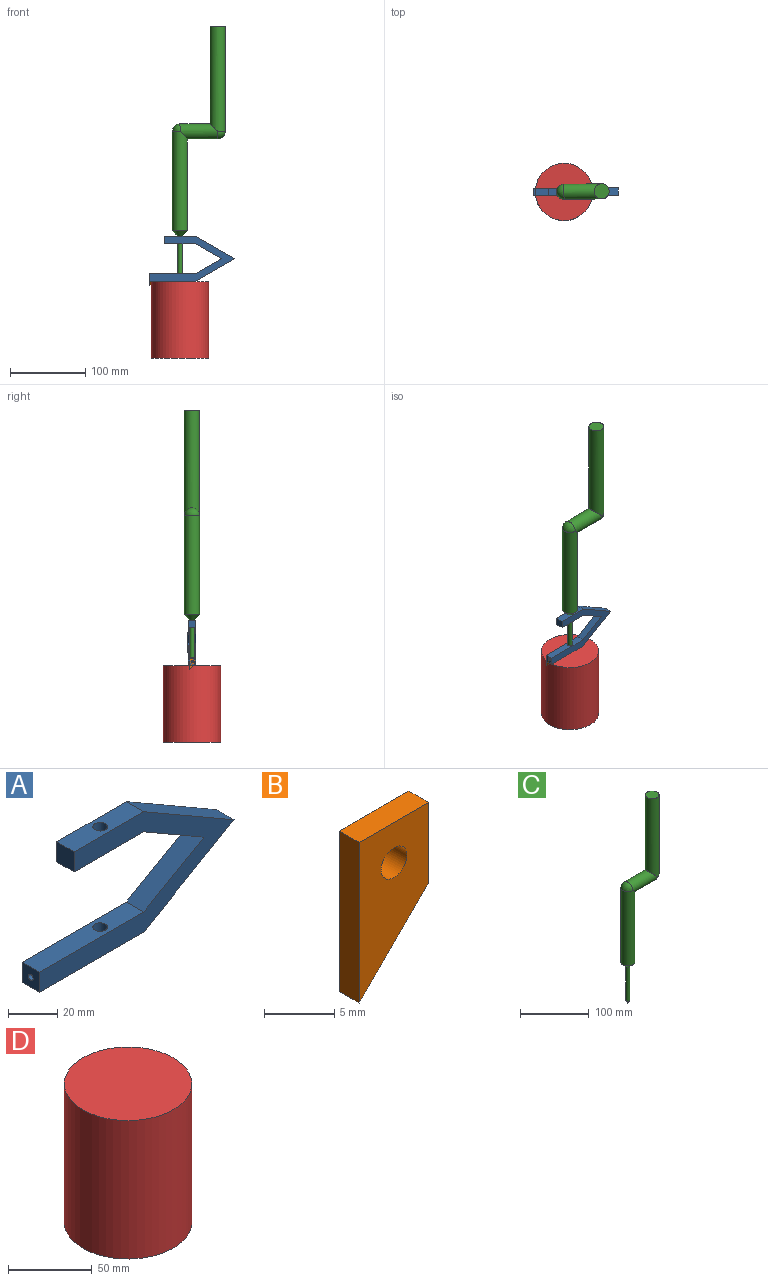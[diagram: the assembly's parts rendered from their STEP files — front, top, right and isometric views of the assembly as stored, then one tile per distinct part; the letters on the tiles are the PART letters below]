
ASSEMBLY  parts=4 mates=3
PART A: 22 faces, bbox 112x10x60 mm
  f0: plane 60x10mm, normal (0,0,-1), area 557.7mm2, adj f3,f4,f10,f11,f12,f13,f14,f15
  f1: plane 34.64x20mm, normal (-0.5,0,0.87), area 400mm2, adj f2,f9,f10,f11
  f2: plane 60x10mm, normal (0,0,1), area 571.7mm2, adj f1,f3,f10,f11,f21
  f3: plane 10x10mm, normal (-1,0,0), area 93.9mm2, adj f0,f2,f10,f11,f17
  f4: plane 51.96x30mm, normal (0.5,0,-0.87), area 600mm2, adj f0,f5,f10,f11
  f5: plane 51.96x30mm, normal (0.5,0,0.87), area 600mm2, adj f4,f6,f10,f11
  f6: plane 40x10mm, normal (0,0,1), area 371.7mm2, adj f5,f7,f10,f11,f20
  f7: plane 10x10mm, normal (-1,0,0), area 100mm2, adj f6,f8,f10,f11
  f8: plane 40x10mm, normal (0,0,-1), area 371.7mm2, adj f7,f9,f10,f11,f20
  f9: plane 34.64x20mm, normal (-0.5,0,-0.87), area 400mm2, adj f1,f8,f10,f11
  f10: plane 111.96x60mm, normal (0,-1,0), area 1866mm2, adj f0,f1,f2,f3,f4,f5,f6,f7
  f11: plane 111.96x60mm, normal (0,1,0), area 1866mm2, adj f0,f1,f2,f3,f4,f5,f6,f7
  f12: plane 7x2mm, normal (0,-1,0), area 14mm2, adj f0,f13,f15,f16
  f13: plane 7x7mm, normal (-1,0,0), area 42.9mm2, adj f0,f12,f14,f16,f18
  f14: plane 7x2mm, normal (0,1,0), area 14mm2, adj f0,f13,f15,f16
  f15: plane 7x7mm, normal (1,0,0), area 42.9mm2, adj f0,f12,f14,f16,f17
  f16: plane 7x2mm, normal (0,0,-1), area 14mm2, adj f12,f13,f14,f15
  f17: cylinder r=1.4mm len=2.79mm, axis (-1,0,0), area 17.6mm2, adj f3,f15
  f18: cylinder r=1.4mm len=6mm, axis (-1,0,0), area 52.7mm2, adj f13,f19
  f19: cone r=0mm half-angle=59deg, axis (-1,0,0), area 7.2mm2, adj f18
  f20: cylinder r=3mm len=10mm, axis (0,0,1), area 188.5mm2, adj f6,f8
  f21: cylinder r=3mm len=10mm, axis (0,0,1), area 188.5mm2, adj f0,f2
PART B: 7 faces, bbox 7x2x14 mm
  f0: plane 7x2mm, normal (1,0,0), area 14mm2, adj f1,f4,f5,f6
  f1: plane 7x2mm, normal (0,0,1), area 14mm2, adj f0,f2,f5,f6
  f2: plane 14x2mm, normal (-1,0,0), area 28mm2, adj f1,f4,f5,f6
  f3: cylinder r=1.3mm len=2.6mm, axis (0,1,0), area 16.3mm2, adj f5,f6
  f4: plane 7x7mm, normal (0.71,0,-0.71), area 19.8mm2, adj f0,f2,f5,f6
  f5: plane 14x7mm, normal (0,-1,0), area 68.2mm2, adj f0,f1,f2,f3,f4
  f6: plane 14x7mm, normal (0,1,0), area 68.2mm2, adj f0,f1,f2,f3,f4
PART C: 9 faces, bbox 70x20x345 mm
  f0: plane 20x20mm, normal (0,0,1), area 314.2mm2, adj f4
  f1: cylinder r=10mm len=132mm, axis (0,0,1), area 8093.8mm2, adj f2,f3,f8
  f2: sphere r=10mm, area 314.2mm2, adj f1,f3
  f3: cylinder r=10mm len=50mm, axis (1,0,0), area 2741.6mm2, adj f1,f2,f4,f5
  f4: cylinder r=10mm len=140mm, axis (0,0,1), area 8596.5mm2, adj f0,f3,f5
  f5: sphere r=10mm, area 314.2mm2, adj f3,f4
  f6: cylinder r=3mm len=60.8mm, axis (0,0,1), area 1146.1mm2, adj f7,f8
  f7: cone r=3mm half-angle=30deg, axis (0,0,1), area 56.5mm2, adj f6
  f8: cone r=2mm half-angle=45deg, axis (0,0,1), area 404.3mm2, adj f1,f6
PART D: 3 faces, bbox 76x76x101 mm
  f0: cylinder r=38mm len=101mm, axis (0,0,-1), area 24114.9mm2, adj f1,f2
  f1: plane 76x76mm, normal (0,0,1), area 4536.5mm2, adj f0
  f2: plane 76x76mm, normal (0,0,-1), area 4536.5mm2, adj f0
PLACE A rot(axis=(0,0,1),0.4deg) t=(19.36,10.41,128.76)mm
PLACE B rot(axis=(0,0,-1),89.6deg) t=(-39.41,-25.74,100.26)mm
PLACE C rot(axis=(0,0,1),0.4deg) t=(24.36,10.45,297.76)mm
PLACE D t=(-0.64,10.28,-3.04)mm fixed
MATE fastened B.f3 <-> A.f17  axis (-1,-0.01,0) through (-40.64,10.02,103.76)mm
MATE revolute D.f0 <-> C.f1  axis (0,0,1) through (-0.64,10.28,97.96)mm
MATE fastened C.f1 <-> A.f20  axis (0,0,1) through (-0.64,10.28,158.76)mm
